# Revit family: YKK_AP_America_Inc_Swing_Door_Model_35D_Pair_Medium_Stile
name_source: partatom
category: Doors
revit_build: Autodesk Revit 2015 (Build: 20150704_0715(x64)
units: mm (PartAtom-declared; Revit-internal decimal feet)

## types (6) — shared parameters
Analytic Construction = <None>
Bottom Rail = 5 5/32"
Door Thickness = 1 3/4"
DoorThickness = 1 3/4"
DoorWidth = 7' - 0"
Function = Interior
Hinge Stile = 4 19/32"
Hinge Stile Rgiht = 4 19/32"
Lever Stile = 4 19/32"
Lever Stile Rgiht = 4 19/32"
Manufacturer = YKK
Model = 20D
Offset = 0"
Top Rail = 4 1/8"
URL = http://www.ykkap.com

## per-type parameters (varying)
| type | DoorHeight | DoorMaterial | DoorType |
| D_WS_AL_84x94 | 0" |  |  |
| D_WS_AL_72x94 | 7' - 10" | AL |  |
| D_WS_AL_76x102 | 7' - 10" | AL | D_WS |
| D_WS_AL_72x102 | 7' - 10" | AL | D_WS |
| D_WS_AL_84x102 | 7' - 10" | AL | D_WS |
| D_WS_AL_76x94 | 7' - 10" | AL |  |

## geometry (parser evidence)
native form markers: Blend x8, Sweep x4
no freeform markers — native parametric forms only
